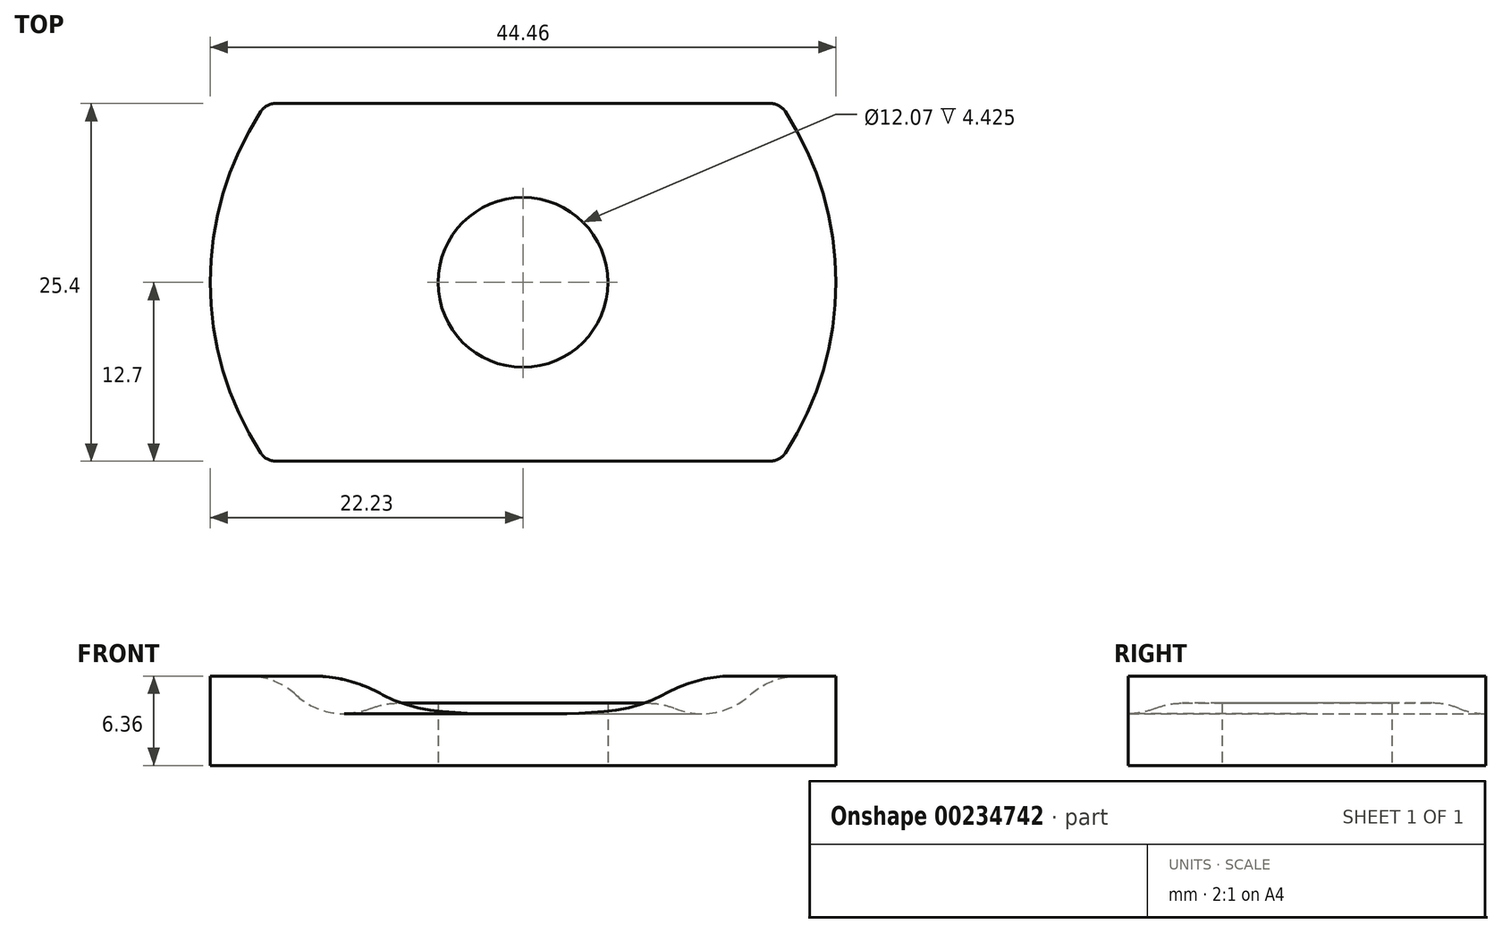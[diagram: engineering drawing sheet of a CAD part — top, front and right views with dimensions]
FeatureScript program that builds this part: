
annotation { "Feature Type Name" : "Feature", "Feature Type Description" : "" }
export const myFeature = defineFeature(function(context is Context, id is Id, definition is map)
    precondition{}
    {
        {
            var Q0;
            Q0=qCreatedBy(makeId("Top.planeOp"),FACE);
            var sketch = newSketch(context, id + "F0", { "sketchPlane" : qUnion([Q0])});
            skArc(sketch, "E0", {"start": v(-18.24, 12.7) * mm, "mid": v(-22.23, 0) * mm, "end": v(-18.24, -12.7) * mm});
            skLineSegment(sketch, "E1.bottom", {"start": v(18.24, 12.7) * mm, "end": v(-18.24, 12.7) * mm});
            skLineSegment(sketch, "E1.top", {"start": v(18.24, -12.7) * mm, "end": v(-18.24, -12.7) * mm});
            skLineSegment(sketch, "E1.left", {"start": v(18.24, 12.7) * mm, "end": v(18.24, -12.7) * mm, "construction": true});
            skLineSegment(sketch, "E1.right", {"start": v(-18.24, 12.7) * mm, "end": v(-18.24, -12.7) * mm, "construction": true});
            skArc(sketch, "E2.trimOffspring", {"start": v(18.24, -12.7) * mm, "mid": v(22.23, 0) * mm, "end": v(18.24, 12.7) * mm});
            skCircle(sketch, "E3", {"center": v(0, 0) * mm, "radius": 6.04 * mm});
            skSolve(sketch);
        }
        {
            var Q0;
            Q0=qSketchRegion(id+"F0",true);
            extrude(context, id + "F1", {"entities" : qUnion([Q0]), "endBound" : BoundingType.SYMMETRIC, "depth" : 6.35 * mm});
        }
        {
            var Q0;
            Q0=qCreatedBy(makeId("Front.planeOp"),FACE);
            var sketch = newSketch(context, id + "F2", { "sketchPlane" : qUnion([Q0])});
            skCircle(sketch, "E4", {"center": v(12.7, 5.58) * mm, "radius": 5.08 * mm});
            skLineSegment(sketch, "E5", {"start": v(12.7, 5.58) * mm, "end": v(12.7, 3.18) * mm});
            skLineSegment(sketch, "E6", {"start": v(12.7, 3.18) * mm, "end": v(12.7, 0.5) * mm});
            skLineSegment(sketch, "E7", {"start": v(8.14, 7.81) * mm, "end": v(0, 7.81) * mm});
            skLineSegment(sketch, "E8", {"start": v(0, 7.81) * mm, "end": v(0, 1.25) * mm});
            skLineSegment(sketch, "E9", {"start": v(0, 1.25) * mm, "end": v(15.36, 1.25) * mm});
            skLineSegment(sketch, "E10", {"start": v(0, 0) * mm, "end": v(-5.27, 0) * mm, "construction": true});
            skSolve(sketch);
        }
        {
            var Q0;
            Q0=qSketchRegion(id+"F2",true);
            var Q1;
            Q1=makeQuery(id+"F1.opExtrude","SWEPT_FACE",FACE,{"disambiguationData":[OSD([sQuery(id+"F0.wireOp",EDGE,"E3")])]});
            revolve(context, id + "F3", {"operationType" : NewBodyOperationType.REMOVE, "entities" : qUnion([Q0]), "axis" : qUnion([Q1]), "revolveType" : RevolveType.FULL, "oppositeDirection" : true});
        }
        {
            var Q0;
            Q0=makeQuery(id+"F3.boolean.opBoolean","INTERSECT",EDGE,{"disambiguationData":[OD(1.0)],"derivedFrom":[makeQuery(id+"F1.opExtrude","CAP_FACE",FACE,{"disambiguationData":[OSD([sQuery(id+"F0.wireOp",EDGE,"E0"),sQuery(id+"F0.wireOp",EDGE,"E1.bottom"),sQuery(id+"F0.wireOp",EDGE,"E1.top"),sQuery(id+"F0.wireOp",EDGE,"E2.trimOffspring"),sQuery(id+"F0.wireOp",EDGE,"E3")])],"isStart":false}),makeQuery(id+"F3.opRevolve","SWEPT_FACE",FACE,{"disambiguationData":[OSD([sQuery(id+"F2.wireOp",EDGE,"E4")])]})]});
            var Q1;
            Q1=makeQuery(id+"F3.boolean.opBoolean","INTERSECT",EDGE,{"disambiguationData":[OD(0.0)],"derivedFrom":[makeQuery(id+"F1.opExtrude","CAP_FACE",FACE,{"disambiguationData":[OSD([sQuery(id+"F0.wireOp",EDGE,"E0"),sQuery(id+"F0.wireOp",EDGE,"E1.bottom"),sQuery(id+"F0.wireOp",EDGE,"E1.top"),sQuery(id+"F0.wireOp",EDGE,"E2.trimOffspring"),sQuery(id+"F0.wireOp",EDGE,"E3")])],"isStart":false}),makeQuery(id+"F3.opRevolve","SWEPT_FACE",FACE,{"disambiguationData":[OSD([sQuery(id+"F2.wireOp",EDGE,"E4")])]})]});
            var Q2;
            Q2=makeQuery(id+"F3.boolean.opBoolean","COPY",EDGE,{"derivedFrom":makeQuery(id+"F3.opRevolve","SWEPT_EDGE",EDGE,{"disambiguationData":[OSD([sQuery(id+"F2.wireOp",EDGE,"E4"),sQuery(id+"F2.wireOp",EDGE,"E9")])]})});
            var Q3;
            Q3=makeQuery(id+"FBVG78wqvWEtJCH_1.1.F3.boolean.opBoolean","INTERSECT",EDGE,{"disambiguationData":[OD(1.0)],"derivedFrom":[makeQuery(id+"F1.opExtrude","CAP_FACE",FACE,{"disambiguationData":[OSD([sQuery(id+"F0.wireOp",EDGE,"E0"),sQuery(id+"F0.wireOp",EDGE,"E1.bottom"),sQuery(id+"F0.wireOp",EDGE,"E1.top"),sQuery(id+"F0.wireOp",EDGE,"E2.trimOffspring"),sQuery(id+"F0.wireOp",EDGE,"E3")])],"isStart":true}),makeQuery(id+"FBVG78wqvWEtJCH_1.1.F3.opRevolve","SWEPT_FACE",FACE,{"disambiguationData":[OSD([sQuery(id+"F2.wireOp",EDGE,"E4")])]})]});
            var Q4;
            Q4=makeQuery(id+"FBVG78wqvWEtJCH_1.1.F3.boolean.opBoolean","COPY",EDGE,{"derivedFrom":makeQuery(id+"FBVG78wqvWEtJCH_1.1.F3.opRevolve","SWEPT_EDGE",EDGE,{"disambiguationData":[OSD([sQuery(id+"F2.wireOp",EDGE,"E4"),sQuery(id+"F2.wireOp",EDGE,"E9")])]})});
            var Q5;
            Q5=makeQuery(id+"FBVG78wqvWEtJCH_1.1.F3.boolean.opBoolean","INTERSECT",EDGE,{"disambiguationData":[OD(0.0)],"derivedFrom":[makeQuery(id+"F1.opExtrude","CAP_FACE",FACE,{"disambiguationData":[OSD([sQuery(id+"F0.wireOp",EDGE,"E0"),sQuery(id+"F0.wireOp",EDGE,"E1.bottom"),sQuery(id+"F0.wireOp",EDGE,"E1.top"),sQuery(id+"F0.wireOp",EDGE,"E2.trimOffspring"),sQuery(id+"F0.wireOp",EDGE,"E3")])],"isStart":true}),makeQuery(id+"FBVG78wqvWEtJCH_1.1.F3.opRevolve","SWEPT_FACE",FACE,{"disambiguationData":[OSD([sQuery(id+"F2.wireOp",EDGE,"E4")])]})]});
            fillet(context, id + "F4", {"entities" : qUnion([Q0, Q1, Q2, Q3, Q4, Q5]), "radius" : 5.08 * mm, "tangentPropagation" : true, "allowEdgeOverflow" : false});
        }
        {
            var Q0;
            Q0=makeQuery(id+"F1.opExtrude","SWEPT_EDGE",EDGE,{"disambiguationData":[OSD([sQuery(id+"F0.wireOp",EDGE,"E0"),sQuery(id+"F0.wireOp",EDGE,"E1.top")])]});
            var Q1;
            Q1=makeQuery(id+"F1.opExtrude","SWEPT_EDGE",EDGE,{"disambiguationData":[OSD([sQuery(id+"F0.wireOp",EDGE,"E0"),sQuery(id+"F0.wireOp",EDGE,"E1.bottom")])]});
            var Q2;
            Q2=makeQuery(id+"F1.opExtrude","SWEPT_EDGE",EDGE,{"disambiguationData":[OSD([sQuery(id+"F0.wireOp",EDGE,"E1.bottom"),sQuery(id+"F0.wireOp",EDGE,"E2.trimOffspring")])]});
            var Q3;
            Q3=makeQuery(id+"F1.opExtrude","SWEPT_EDGE",EDGE,{"disambiguationData":[OSD([sQuery(id+"F0.wireOp",EDGE,"E1.top"),sQuery(id+"F0.wireOp",EDGE,"E2.trimOffspring")])]});
            fillet(context, id + "F5", {"entities" : qUnion([Q0, Q1, Q2, Q3]), "radius" : 1.27 * mm, "tangentPropagation" : true, "allowEdgeOverflow" : false});
        }
    });
